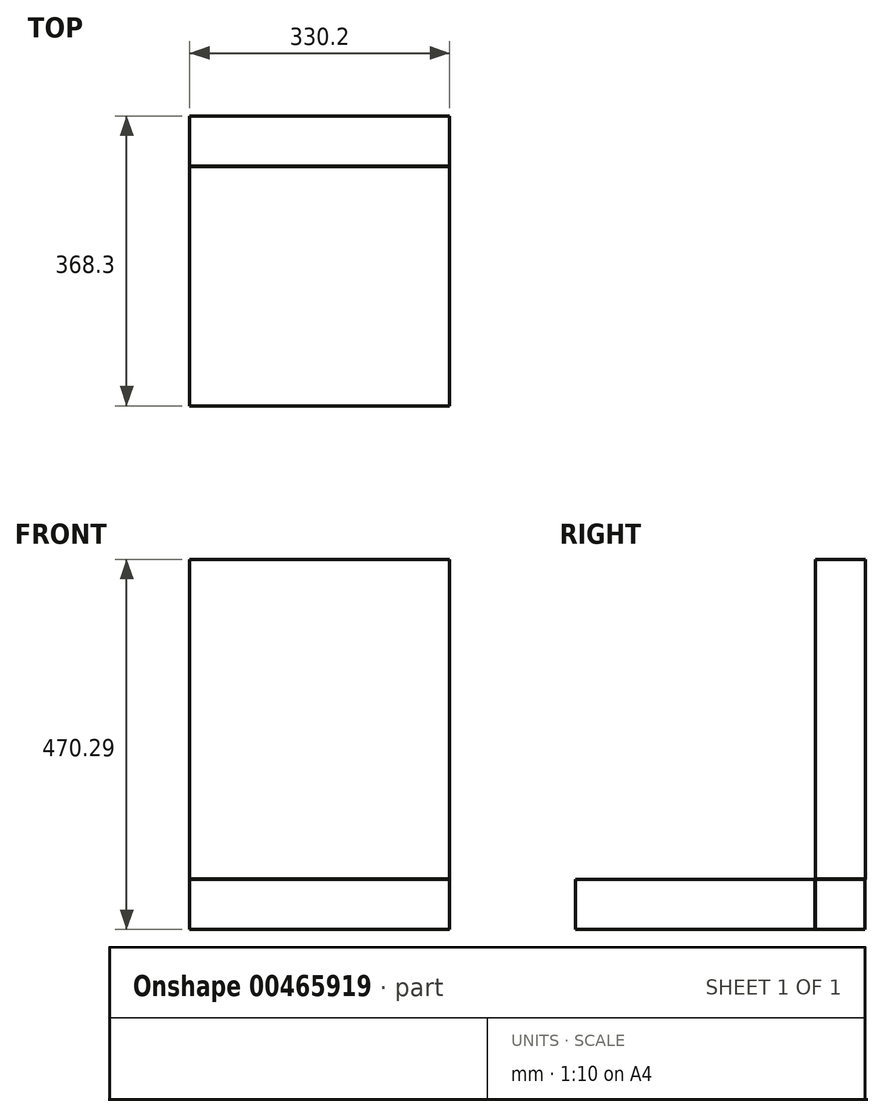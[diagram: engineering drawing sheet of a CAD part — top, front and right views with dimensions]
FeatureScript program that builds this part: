
annotation { "Feature Type Name" : "Feature", "Feature Type Description" : "" }
export const myFeature = defineFeature(function(context is Context, id is Id, definition is map)
    precondition{}
    {
        {
            var Q0;
            Q0=qCreatedBy(makeId("Top.planeOp"),FACE);
            var sketch = newSketch(context, id + "F0", { "sketchPlane" : qUnion([Q0])});
            skLineSegment(sketch, "E0.bottom", {"start": v(-165.1, 150.22) * mm, "end": v(165.1, 150.22) * mm});
            skLineSegment(sketch, "E0.top", {"start": v(-165.1, -154.58) * mm, "end": v(165.1, -154.58) * mm});
            skLineSegment(sketch, "E0.left", {"start": v(-165.1, 150.22) * mm, "end": v(-165.1, -154.58) * mm});
            skLineSegment(sketch, "E0.right", {"start": v(165.1, 150.22) * mm, "end": v(165.1, -154.58) * mm});
            skPoint(sketch, "E0.middle", {"position": v(0, -2.18) * mm});
            skSolve(sketch);
        }
        {
            var Q0;
            Q0=makeQuery(id+"F0.imprint","IMPRINT",FACE,{"disambiguationData":[TD([[makeQuery(id+"F0.imprint","IMPRINT",EDGE,{"derivedFrom":sQuery(id+"F0.wireOp",EDGE,"E0.bottom")}),-1.0]])]});
            extrude(context, id + "F1", {"entities" : qUnion([Q0]), "endBound" : BoundingType.SYMMETRIC, "depth" : 63.5 * mm});
        }
        {
            var Q0;
            Q0=makeQuery(id+"F1.opExtrude","CAP_FACE",FACE,{"disambiguationData":[OSD([sQuery(id+"F0.wireOp",EDGE,"E0.bottom"),sQuery(id+"F0.wireOp",EDGE,"E0.top"),sQuery(id+"F0.wireOp",EDGE,"E0.left"),sQuery(id+"F0.wireOp",EDGE,"E0.right")])],"isStart":false});
            var sketch = newSketch(context, id + "F2", { "sketchPlane" : qUnion([Q0])});
            skLineSegment(sketch, "E1", {"start": v(-165.1, 150.22) * mm, "end": v(-165.1, 213.72) * mm});
            skLineSegment(sketch, "E2", {"start": v(-165.1, 213.72) * mm, "end": v(165.1, 213.72) * mm});
            skLineSegment(sketch, "E3", {"start": v(165.1, 213.72) * mm, "end": v(165.1, 150.22) * mm});
            skSolve(sketch);
        }
        {
            var Q0;
            Q0=makeQuery(id+"F2.imprint","IMPRINT",FACE,{"disambiguationData":[TD([[makeQuery(id+"F2.imprint","IMPRINT",EDGE,{"derivedFrom":sQuery(id+"F2.wireOp",EDGE,"E1")}),-1.0]])]});
            extrude(context, id + "F3", {"entities" : qUnion([Q0]), "operationType" : NewBodyOperationType.ADD, "depth" : 406.4 * mm});
        }
        {
            var Q0;
            Q0=qCreatedBy(makeId("Right.planeOp"),FACE);
            var sketch = newSketch(context, id + "F4", { "sketchPlane" : qUnion([Q0])});
            skLineSegment(sketch, "E4", {"start": v(0, 0) * mm, "end": v(180.98, 0) * mm});
            skLineSegment(sketch, "E5.bottom", {"start": v(149.2, 32.14) * mm, "end": v(212.74, 32.14) * mm});
            skLineSegment(sketch, "E5.top", {"start": v(149.2, -32.14) * mm, "end": v(212.74, -32.14) * mm});
            skLineSegment(sketch, "E5.left", {"start": v(149.2, 32.14) * mm, "end": v(149.2, -32.14) * mm});
            skLineSegment(sketch, "E5.right", {"start": v(212.74, 32.14) * mm, "end": v(212.74, -32.14) * mm});
            skPoint(sketch, "E5.middle", {"position": v(180.98, 0) * mm});
            skSolve(sketch);
        }
        {
            var Q0;
            {var subQ0=sQuery(id+"F4.wireOp",EDGE,"E5.bottom");Q0=makeQuery(id+"F4.imprint","IMPRINT",FACE,{"disambiguationData":[TD([[makeQuery(id+"F4.imprint","IMPRINT",EDGE,{"derivedFrom":subQ0}),-1.0]])]});}
            extrude(context, id + "F5", {"entities" : qUnion([Q0]), "endBound" : BoundingType.SYMMETRIC, "depth" : 330.2 * mm});
        }
    });
